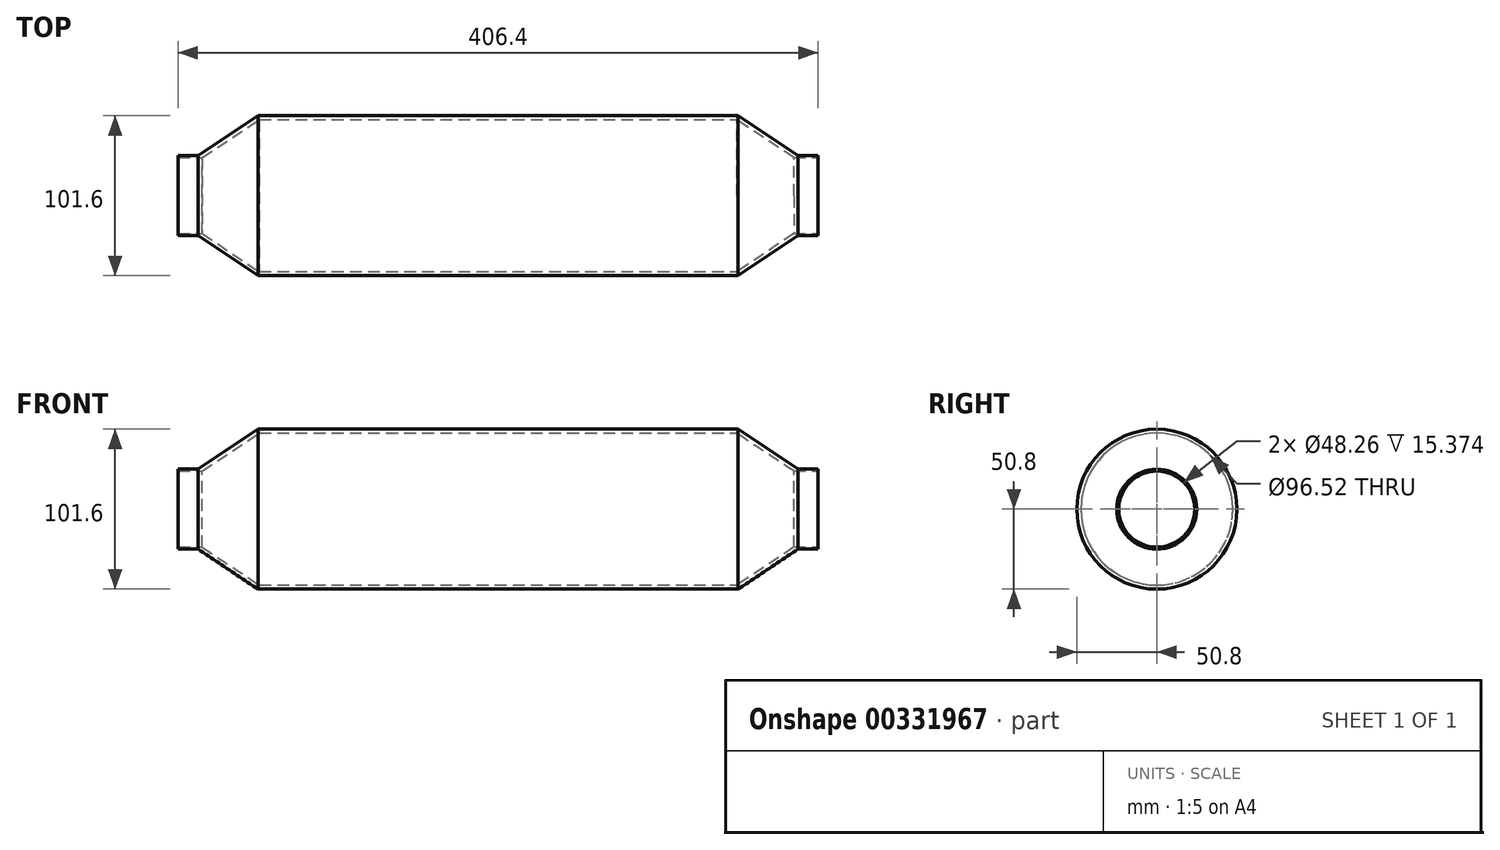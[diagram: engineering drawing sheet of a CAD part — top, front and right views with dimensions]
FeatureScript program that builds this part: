
annotation { "Feature Type Name" : "Feature", "Feature Type Description" : "" }
export const myFeature = defineFeature(function(context is Context, id is Id, definition is map)
    precondition{}
    {
        {
            var Q0;
            Q0=qCreatedBy(makeId("Front.planeOp"),FACE);
            var sketch = newSketch(context, id + "F0", { "sketchPlane" : qUnion([Q0])});
            skLineSegment(sketch, "E0", {"start": v(-115.68, 0) * mm, "end": v(-115.68, 25.4) * mm});
            skLineSegment(sketch, "E1", {"start": v(-115.68, 25.4) * mm, "end": v(-102.98, 25.4) * mm});
            skLineSegment(sketch, "E2", {"start": v(-102.98, 25.4) * mm, "end": v(-64.88, 50.8) * mm});
            skLineSegment(sketch, "E3", {"start": v(-64.88, 50.8) * mm, "end": v(239.92, 50.8) * mm});
            skLineSegment(sketch, "E4", {"start": v(239.92, 50.8) * mm, "end": v(278.02, 25.4) * mm});
            skLineSegment(sketch, "E5", {"start": v(278.02, 25.4) * mm, "end": v(290.72, 25.4) * mm});
            skLineSegment(sketch, "E6", {"start": v(290.72, 25.4) * mm, "end": v(290.72, 0) * mm});
            skLineSegment(sketch, "E7", {"start": v(290.72, 0) * mm, "end": v(-115.68, 0) * mm});
            skSolve(sketch);
        }
        {
            var Q0;
            Q0 = qSketchRegion(id + "F0", true);
            var Q1;
            Q1=sQuery(id+"F0.wireOp",EDGE,"E1");
            var Q2;
            Q2=sQuery(id+"F0.wireOp",EDGE,"E2");
            var Q3;
            Q3=sQuery(id+"F0.wireOp",EDGE,"E3");
            var Q4;
            Q4=sQuery(id+"F0.wireOp",EDGE,"E4");
            var Q5;
            Q5=sQuery(id+"F0.wireOp",EDGE,"E5");
            var Q6;
            Q6=sQuery(id+"F0.wireOp",EDGE,"E7");
            revolve(context, id + "F1", {"entities" : qUnion([Q0]), "surfaceEntities" : qUnion([Q1, Q2, Q3, Q4, Q5]), "axis" : qUnion([Q6]), "revolveType" : RevolveType.FULL});
        }
        {
            var Q0;
            Q0=makeQuery(id+"F1.opRevolve","SWEPT_FACE",FACE,{"disambiguationData":[OSD([sQuery(id+"F0.wireOp",EDGE,"E0")])]});
            shell(context, id + "F2", {"entities" : qUnion([Q0]), "thickness" : 2.54 * mm});
        }
        {
            var Q0;
            Q0=makeQuery(id+"F1.opRevolve","SWEPT_FACE",FACE,{"disambiguationData":[OSD([sQuery(id+"F0.wireOp",EDGE,"E6")])]});
            var sketch = newSketch(context, id + "F3", { "sketchPlane" : qUnion([Q0])});
            skCircle(sketch, "E8", {"center": v(0, 0) * mm, "radius": 24.13 * mm});
            skSolve(sketch);
        }
        {
            var Q0;
            Q0=sQuery(id+"F3.wireOp",VERTEX,"E8.center");
            var Q1;
            Q1=makeQuery(id+"F1.opRevolve","SWEPT_BODY",BODY,{"disambiguationData":[OSD([sQuery(id+"F0.wireOp",EDGE,"E0"),sQuery(id+"F0.wireOp",EDGE,"E1"),sQuery(id+"F0.wireOp",EDGE,"E2"),sQuery(id+"F0.wireOp",EDGE,"E3"),sQuery(id+"F0.wireOp",EDGE,"E4"),sQuery(id+"F0.wireOp",EDGE,"E5"),sQuery(id+"F0.wireOp",EDGE,"E6"),sQuery(id+"F0.wireOp",EDGE,"E7")])]});
            hole(context, id + "F4", {"style" : HoleStyle.SIMPLE, "endStyle" : HoleEndStyle.THROUGH, "holeDiameter" : 48.26 * mm, "tappedDepth" : 12.7 * mm, "tapClearance" : 3, "locations" : qUnion([Q0]), "scope" : qUnion([Q1])});
        }
    });
